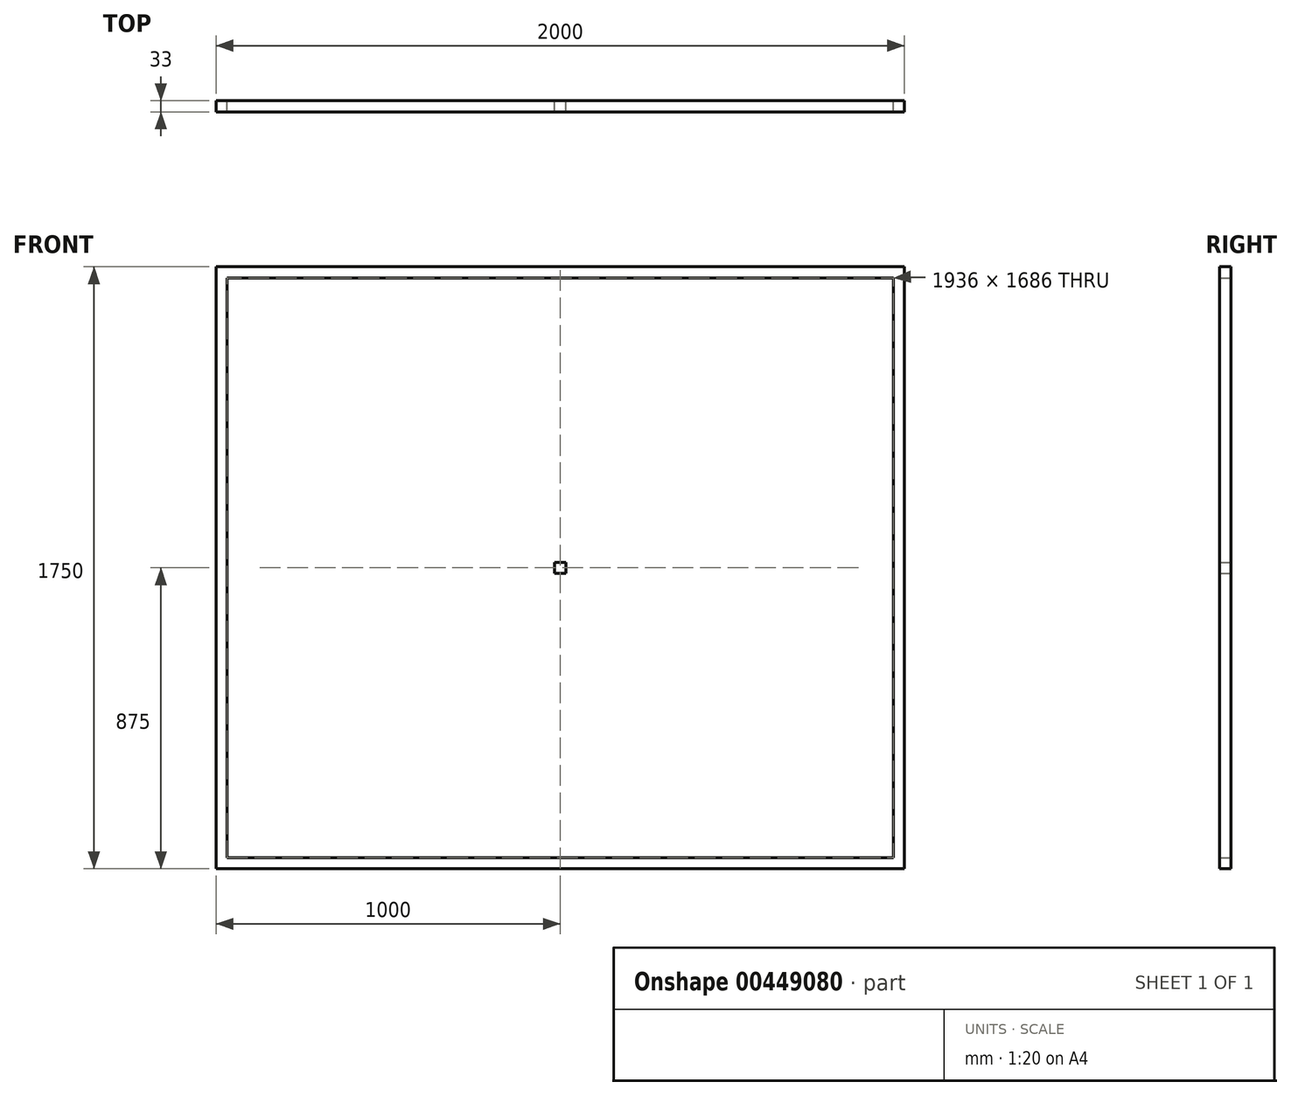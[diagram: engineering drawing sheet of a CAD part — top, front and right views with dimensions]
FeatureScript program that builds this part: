
annotation { "Feature Type Name" : "Feature", "Feature Type Description" : "" }
export const myFeature = defineFeature(function(context is Context, id is Id, definition is map)
    precondition{}
    {
        {
            var Q0;
            Q0=qCreatedBy(makeId("Front.planeOp"),FACE);
            var sketch = newSketch(context, id + "F0", { "sketchPlane" : qUnion([Q0])});
            skLineSegment(sketch, "E0.bottom", {"start": v(0, 0) * mm, "end": v(2000, 0) * mm});
            skLineSegment(sketch, "E0.top", {"start": v(0, 1750) * mm, "end": v(2000, 1750) * mm});
            skLineSegment(sketch, "E0.left", {"start": v(0, 0) * mm, "end": v(0, 1750) * mm});
            skLineSegment(sketch, "E0.right", {"start": v(2000, 0) * mm, "end": v(2000, 1750) * mm});
            skLineSegment(sketch, "E1.0", {"start": v(32, 32) * mm, "end": v(32, 1718) * mm});
            skLineSegment(sketch, "E1.1", {"start": v(32, 32) * mm, "end": v(1968, 32) * mm});
            skLineSegment(sketch, "E1.2", {"start": v(1968, 32) * mm, "end": v(1968, 1718) * mm});
            skLineSegment(sketch, "E1.3", {"start": v(32, 1718) * mm, "end": v(1968, 1718) * mm});
            skLineSegment(sketch, "E2", {"start": v(1000, 1718) * mm, "end": v(1000, 32) * mm, "construction": true});
            skLineSegment(sketch, "E3", {"start": v(32, 875) * mm, "end": v(1968, 875) * mm, "construction": true});
            skLineSegment(sketch, "E4.bottom", {"start": v(984, 1718) * mm, "end": v(1016, 1718) * mm});
            skLineSegment(sketch, "E4.top", {"start": v(984, 32) * mm, "end": v(1016, 32) * mm});
            skLineSegment(sketch, "E4.left", {"start": v(984, 1718) * mm, "end": v(984, 32) * mm});
            skLineSegment(sketch, "E4.right", {"start": v(1016, 1718) * mm, "end": v(1016, 32) * mm});
            skLineSegment(sketch, "E5.bottom", {"start": v(1968, 891) * mm, "end": v(32, 891) * mm});
            skLineSegment(sketch, "E5.top", {"start": v(1968, 859) * mm, "end": v(32, 859) * mm});
            skLineSegment(sketch, "E5.left", {"start": v(1968, 891) * mm, "end": v(1968, 859) * mm});
            skLineSegment(sketch, "E5.right", {"start": v(32, 891) * mm, "end": v(32, 859) * mm});
            skLineSegment(sketch, "E6", {"start": v(1968, 875) * mm, "end": v(1926.84, 875) * mm, "construction": true});
            skLineSegment(sketch, "E7", {"start": v(1000, 1718) * mm, "end": v(1000, 1691.84) * mm, "construction": true});
            skSolve(sketch);
        }
        {
            var Q0;
            Q0=qSketchRegion(id+"F0",true);
            var Q1;
            {var subQ5=sQuery(id+"F0.wireOp",EDGE,"E5.right");Q1=makeQuery(id+"F0.imprint","IMPRINT",FACE,{"disambiguationData":[TD([[makeQuery(id+"F0.imprint","IMPRINT",EDGE,{"derivedFrom":subQ5}),1.0]])]});}
            var Q2;
            {var subQ0=sQuery(id+"F0.wireOp",EDGE,"E4.bottom");Q2=makeQuery(id+"F0.imprint","IMPRINT",FACE,{"disambiguationData":[TD([[makeQuery(id+"F0.imprint","IMPRINT",EDGE,{"derivedFrom":subQ0}),-1.0]])]});}
            var Q3;
            {var subQ0=sQuery(id+"F0.wireOp",EDGE,"E5.bottom");var subQ1=sQuery(id+"F0.wireOp",EDGE,"E4.left");var subQ2=makeQuery(id+"F0.imprint","INTERSECT",VERTEX,{"derivedFrom":[subQ1,subQ0]});Q3=makeQuery(id+"F0.imprint","IMPRINT",FACE,{"disambiguationData":[TD([[makeQuery(id+"F0.imprint","IMPRINT",EDGE,{"disambiguationData":[TD([[subQ2,-1.0]])],"derivedFrom":subQ1}),1.0]])]});}
            var Q4;
            {var subQ5=sQuery(id+"F0.wireOp",EDGE,"E5.left");Q4=makeQuery(id+"F0.imprint","IMPRINT",FACE,{"disambiguationData":[TD([[makeQuery(id+"F0.imprint","IMPRINT",EDGE,{"derivedFrom":subQ5}),-1.0]])]});}
            var Q5;
            {var subQ0=sQuery(id+"F0.wireOp",EDGE,"E4.top");Q5=makeQuery(id+"F0.imprint","IMPRINT",FACE,{"disambiguationData":[TD([[makeQuery(id+"F0.imprint","IMPRINT",EDGE,{"derivedFrom":subQ0}),1.0]])]});}
            extrude(context, id + "F1", {"entities" : qUnion([Q0, Q1, Q2, Q3, Q4, Q5]), "depth" : 33 * mm});
        }
    });
